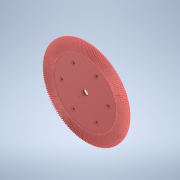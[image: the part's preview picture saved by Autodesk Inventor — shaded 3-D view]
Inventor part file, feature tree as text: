
AUTODESK INVENTOR PART (.ipt)
format: ipt  version: 2021 (Build 250183000, 183)  size: 2,207,744 bytes
history: native  units: mm
features: other x24, pattern_circular x3, sketch x3, loft x2, hole x1, extrude x1
ambient origin geometry x6: Origin, XZ Plane, X Axis, Y Axis, Z Axis, Center Point
bodies: Solid1 (feature_tree)
feature tree (34):
  other  "Top Point"
  other  "Mesh Plane2"
  other  "Teeth Body"
  other  "Start Point"
  other  "Tooth Plane"
  other  "Start Sketch"
  other  "End Point"
  other  "3D Sketch Right"
  other  "End Plane Right"
  loft  "Loft Right"
  pattern_circular  "Circular Pattern Right"  [2 undecoded]
  other  "3D Sketch Left"
  other  "End Plane Left"
  loft  "Loft Left"
  pattern_circular  "Circular Pattern Left"  [2 undecoded]
  other  "Fix Body"
  hole  "Hole1"  [1 undecoded]
  pattern_circular  "Circular Pattern4"  [2 undecoded]
  extrude  "Extrusion1"  Depth=6.35mm
  other  "Mesh Plane"
  other  "Top Plane"
  other  "Teeth Body Sketch"
  other  "End Plane"
  other  "End Sketch"
  other  "Helical Curve Left"
  other  "End Sketch Left"
  other  "Body Sketch"
  sketch  "Sketch6"  dims[d0=190.5mm d1=190.082427mm]
  other  "Srf1"
  other  "Helical Curve Right"
  other  "End Sketch Right"
  sketch  "Sketch8"  dims[d2=190.847978mm]
  sketch  "Sketch9"  dims[d3=25.4mm d4=14.831066mm d5=90.0deg d7=198.531719mm d8=188.414636mm d9=514.364825mm d11=25.516417mm d12=146.070909mm d15=138.627204mm d16=378.44702mm d17=0.0mm d18=90.0deg d19=0.0mm d20=90.0deg d21=1800.0mm d22=360.0deg d26=391.538189mm d27=4.194873mm d28=190.5mm d29=-14.056476mm d30=146.070909mm d31=138.627204mm d32=378.44702mm d35=0.0mm d37=0.0mm d39=0.0mm d40=90.0deg d41=1800.0mm d42=360.0deg d46=90.0deg d47=90.0deg d48=0.0mm d49=0.0mm d50=90.0deg d51=0.174533mm d52=0.0mm d53=0.0mm d54=0.0mm d56=11.639299mm d57=581.139965mm d58=577.833731mm d59=427.577232mm d60=425.144651mm d61=427.577232mm d62=425.144651mm d63=90.0deg d64=90.0deg d65=391.538189mm d66=31.5mm d67=190.5mm d68=-14.056476mm d69=4.194873mm d70=138.627204mm d71=378.44702mm d72=146.070909mm d73=425.144651mm d74=427.577232mm d75=0.0mm d76=90.0deg d77=0.0mm d78=90.0deg d79=0.0mm d80=90.0deg d81=1800.0mm d82=360.0deg d84=10.0mm d85=20.0mm d86=20.0mm d87=10.0mm d88=0.0mm d89=0.0mm d90=6.7564mm d91=19.05mm d92=11.1125mm d93=6.35mm d94=14.3117mm d95=25.4mm d96=0.0mm d97=50.8mm d98=60.0mm d99=360.0deg d101=12.7mm d102=0.0mm d103=0.0mm d100=19.05mm]
  other  "Pitch Diameter"
note: 7 required parameter values undecoded (feature->parameter linkage not recoverable at this tier; creation-order binding heuristic only, values carry confidence <= 0.55)
